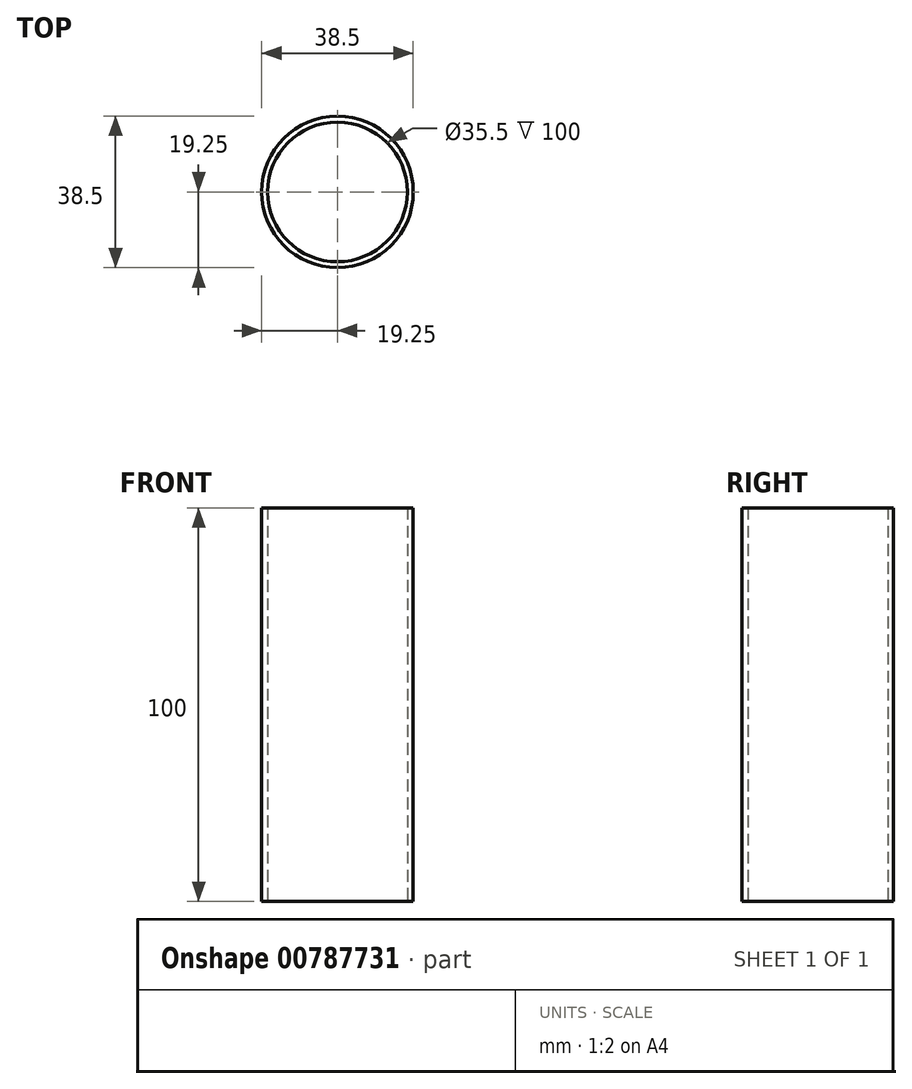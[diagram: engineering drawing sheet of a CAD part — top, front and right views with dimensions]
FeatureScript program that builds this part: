
annotation { "Feature Type Name" : "Feature", "Feature Type Description" : "" }
export const myFeature = defineFeature(function(context is Context, id is Id, definition is map)
    precondition{}
    {
        {
            var Q0;
            Q0=qCreatedBy(makeId("Top.planeOp"),FACE);
            var sketch = newSketch(context, id + "F0", { "sketchPlane" : qUnion([Q0])});
            skCircle(sketch, "E0", {"center": v(0, 0) * mm, "radius": 19.25 * mm});
            skCircle(sketch, "E1", {"center": v(0, 0) * mm, "radius": 17.75 * mm});
            skSolve(sketch);
        }
        {
            var Q0;
            Q0=makeQuery(id+"F0.imprint","IMPRINT",FACE,{"disambiguationData":[TD([[makeQuery(id+"F0.imprint","IMPRINT",EDGE,{"derivedFrom":sQuery(id+"F0.wireOp",EDGE,"E0")}),1.0]])]});
            extrude(context, id + "F1", {"entities" : qUnion([Q0]), "depth" : 100 * mm, "offsetDistance" : 25 * mm});
        }
    });
